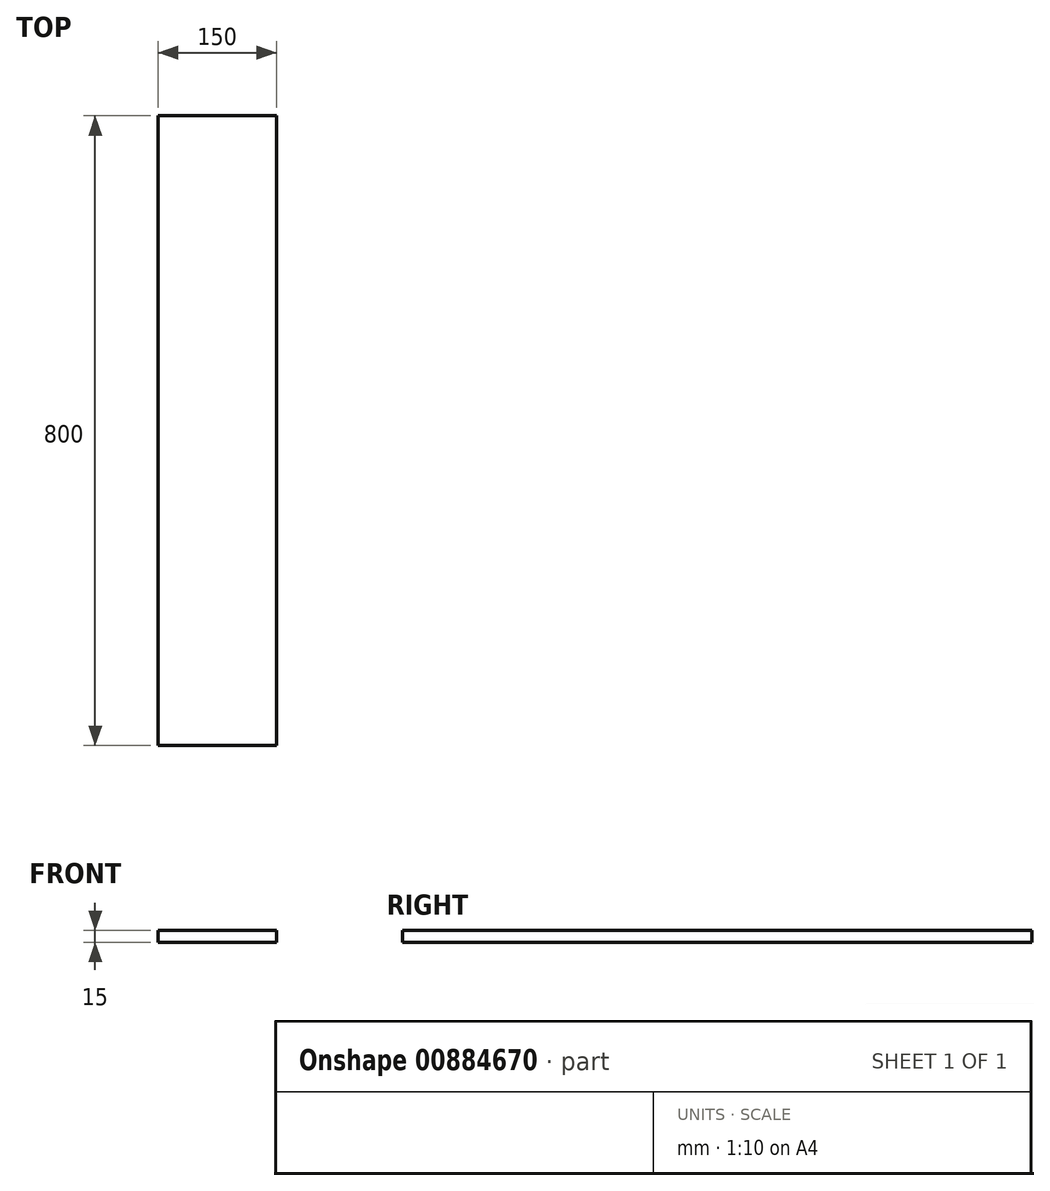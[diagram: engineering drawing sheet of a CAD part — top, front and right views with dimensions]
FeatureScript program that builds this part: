
annotation { "Feature Type Name" : "Feature", "Feature Type Description" : "" }
export const myFeature = defineFeature(function(context is Context, id is Id, definition is map)
    precondition{}
    {
        {
            var Q0;
            Q0=qCreatedBy(makeId("Top.planeOp"),FACE);
            var sketch = newSketch(context, id + "F0", { "sketchPlane" : qUnion([Q0])});
            skLineSegment(sketch, "E0.bottom", {"start": v(75, 400) * mm, "end": v(-75, 400) * mm});
            skLineSegment(sketch, "E0.top", {"start": v(75, -400) * mm, "end": v(-75, -400) * mm});
            skLineSegment(sketch, "E0.left", {"start": v(75, 400) * mm, "end": v(75, -400) * mm});
            skLineSegment(sketch, "E0.right", {"start": v(-75, 400) * mm, "end": v(-75, -400) * mm});
            skPoint(sketch, "E0.middle", {"position": v(0, 0) * mm});
            skSolve(sketch);
        }
        {
            var Q0;
            Q0 = qSketchRegion(id + "F0", true);
            extrude(context, id + "F1", {"entities" : qUnion([Q0]), "depth" : 15 * mm, "offsetDistance" : 25 * mm});
        }
    });
